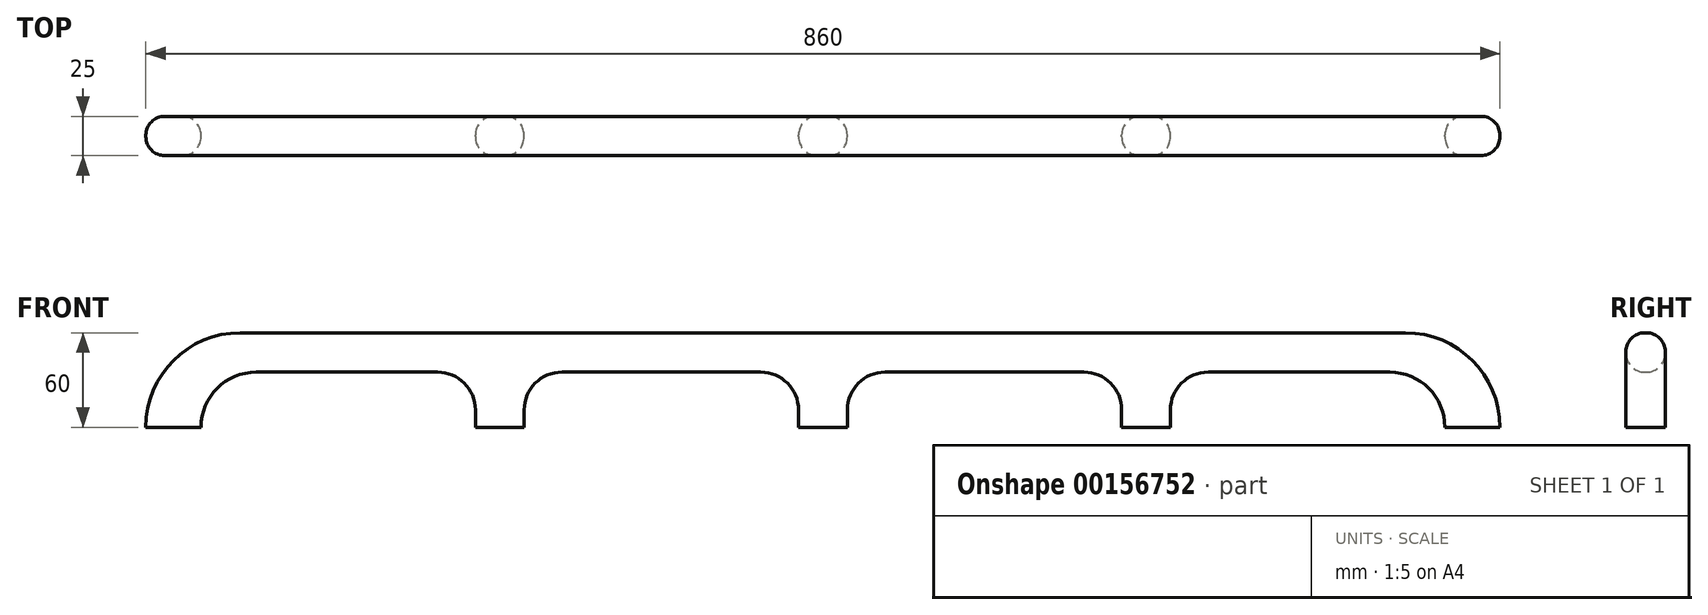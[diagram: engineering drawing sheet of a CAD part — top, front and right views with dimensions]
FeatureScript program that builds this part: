
annotation { "Feature Type Name" : "Feature", "Feature Type Description" : "" }
export const myFeature = defineFeature(function(context is Context, id is Id, definition is map)
    precondition{}
    {
        {
            var Q0;
            Q0=qCreatedBy(makeId("Front.planeOp"),FACE);
            var sketch = newSketch(context, id + "F0", { "sketchPlane" : qUnion([Q0])});
            skLineSegment(sketch, "E0.bottom", {"start": v(-370, 30) * mm, "end": v(0, 30) * mm});
            skLineSegment(sketch, "E0.top", {"start": v(-430, -30) * mm, "end": v(-395, -30) * mm});
            skLineSegment(sketch, "E0.left", {"start": v(-430, -30) * mm, "end": v(-430, -30) * mm});
            skLineSegment(sketch, "E0.right", {"start": v(430, 30) * mm, "end": v(430, -30) * mm, "construction": true});
            skPoint(sketch, "E0.middle", {"position": v(0, 0) * mm});
            skLineSegment(sketch, "E1.0", {"start": v(-395, -30) * mm, "end": v(-395, -30) * mm});
            skLineSegment(sketch, "E2", {"start": v(0, 30) * mm, "end": v(0, -30) * mm, "construction": true});
            skLineSegment(sketch, "E3.0", {"start": v(-15.5, -19) * mm, "end": v(-15.5, -30) * mm, "construction": true});
            skLineSegment(sketch, "E4.0", {"start": v(-360, 5) * mm, "end": v(-244.75, 5) * mm});
            skLineSegment(sketch, "E5.trimOffspring", {"start": v(-15.5, -30) * mm, "end": v(430, -30) * mm, "construction": true});
            skLineSegment(sketch, "E6", {"start": v(-395, -30) * mm, "end": v(-15.5, -30) * mm, "construction": true});
            skLineSegment(sketch, "E7", {"start": v(-205.25, -30) * mm, "end": v(-205.25, 30) * mm, "construction": true});
            skLineSegment(sketch, "E8.0", {"start": v(-220.75, -30) * mm, "end": v(-220.75, -19) * mm});
            skLineSegment(sketch, "E9.0", {"start": v(-189.75, -30) * mm, "end": v(-189.75, -19) * mm});
            skLineSegment(sketch, "E10.trimOffspring", {"start": v(-165.75, 5) * mm, "end": v(-39.5, 5) * mm});
            skLineSegment(sketch, "E11.trimOffspring", {"start": v(0, 5) * mm, "end": v(450, 5) * mm, "construction": true});
            skArc(sketch, "E12.filletArc", {"start": v(-360, 5) * mm, "mid": v(-384.75, -5.25) * mm, "end": v(-395, -30) * mm});
            skArc(sketch, "E13.filletArc", {"start": v(-220.75, -19) * mm, "mid": v(-227.78, -2.03) * mm, "end": v(-244.75, 5) * mm});
            skArc(sketch, "E14.filletArc", {"start": v(-165.75, 5) * mm, "mid": v(-182.72, -2.03) * mm, "end": v(-189.75, -19) * mm});
            skArc(sketch, "E15.filletArc", {"start": v(-15.5, -19) * mm, "mid": v(-22.53, -2.03) * mm, "end": v(-39.5, 5) * mm});
            skPoint(sketch, "E16.visualSharp", {"position": v(-430, 30) * mm});
            skArc(sketch, "E16.filletArc", {"start": v(-370, 30) * mm, "mid": v(-412.43, 12.43) * mm, "end": v(-430, -30) * mm});
            skLineSegment(sketch, "E17", {"start": v(-220.75, -30) * mm, "end": v(-189.75, -30) * mm});
            skLineSegment(sketch, "E18", {"start": v(-15.5, -30) * mm, "end": v(0, -30) * mm});
            skLineSegment(sketch, "E19", {"start": v(-15.5, -19) * mm, "end": v(-15.5, -30) * mm});
            skLineSegment(sketch, "E20.MirrorCS", {"start": v(370, 30) * mm, "end": v(0, 30) * mm});
            skArc(sketch, "E21.MirrorCS", {"start": v(370, 30) * mm, "mid": v(412.43, 12.43) * mm, "end": v(430, -30) * mm});
            skLineSegment(sketch, "E22.MirrorCS", {"start": v(430, -30) * mm, "end": v(395, -30) * mm});
            skArc(sketch, "E23.MirrorCS", {"start": v(360, 5) * mm, "mid": v(384.75, -5.25) * mm, "end": v(395, -30) * mm});
            skLineSegment(sketch, "E24.MirrorCS", {"start": v(360, 5) * mm, "end": v(244.75, 5) * mm});
            skArc(sketch, "E25.MirrorCS", {"start": v(220.75, -19) * mm, "mid": v(227.78, -2.03) * mm, "end": v(244.75, 5) * mm});
            skLineSegment(sketch, "E26.MirrorCS", {"start": v(220.75, -30) * mm, "end": v(220.75, -19) * mm});
            skLineSegment(sketch, "E27.MirrorCS", {"start": v(220.75, -30) * mm, "end": v(189.75, -30) * mm});
            skLineSegment(sketch, "E28.MirrorCS", {"start": v(189.75, -30) * mm, "end": v(189.75, -19) * mm});
            skArc(sketch, "E29.MirrorCS", {"start": v(165.75, 5) * mm, "mid": v(182.72, -2.03) * mm, "end": v(189.75, -19) * mm});
            skLineSegment(sketch, "E30.MirrorCS", {"start": v(165.75, 5) * mm, "end": v(39.5, 5) * mm});
            skArc(sketch, "E31.MirrorCS", {"start": v(15.5, -19) * mm, "mid": v(22.53, -2.03) * mm, "end": v(39.5, 5) * mm});
            skLineSegment(sketch, "E32.MirrorCS", {"start": v(15.5, -19) * mm, "end": v(15.5, -30) * mm});
            skLineSegment(sketch, "E33.MirrorCS", {"start": v(15.5, -30) * mm, "end": v(0, -30) * mm});
            skSolve(sketch);
        }
        {
            var Q0;
            Q0=makeQuery(id+"F0.imprint","IMPRINT",FACE,{"disambiguationData":[TD([[makeQuery(id+"F0.imprint","IMPRINT",EDGE,{"derivedFrom":sQuery(id+"F0.wireOp",EDGE,"E0.bottom")}),-1.0]])]});
            extrude(context, id + "F1", {"entities" : qUnion([Q0]), "depth" : 25 * mm, "symmetric" : true});
        }
        {
            var Q0;
            Q0=makeQuery(id+"F1.opExtrude","CAP_EDGE",EDGE,{"disambiguationData":[OSD([sQuery(id+"F0.wireOp",EDGE,"E12.filletArc")])],"isStart":false});
            var Q1;
            Q1=makeQuery(id+"F1.opExtrude","CAP_EDGE",EDGE,{"disambiguationData":[OSD([sQuery(id+"F0.wireOp",EDGE,"E14.filletArc")])],"isStart":false});
            var Q2;
            Q2=makeQuery(id+"F1.opExtrude","CAP_EDGE",EDGE,{"disambiguationData":[OSD([sQuery(id+"F0.wireOp",EDGE,"E31.MirrorCS")])],"isStart":false});
            var Q3;
            Q3=makeQuery(id+"F1.opExtrude","CAP_EDGE",EDGE,{"disambiguationData":[OSD([sQuery(id+"F0.wireOp",EDGE,"E25.MirrorCS")])],"isStart":false});
            var Q4;
            Q4=makeQuery(id+"F1.opExtrude","CAP_EDGE",EDGE,{"disambiguationData":[OSD([sQuery(id+"F0.wireOp",EDGE,"E21.MirrorCS")])],"isStart":false});
            var Q5;
            Q5=makeQuery(id+"F1.opExtrude","CAP_EDGE",EDGE,{"disambiguationData":[OSD([sQuery(id+"F0.wireOp",EDGE,"E16.filletArc")])],"isStart":true});
            var Q6;
            Q6=makeQuery(id+"F1.opExtrude","CAP_EDGE",EDGE,{"disambiguationData":[OSD([sQuery(id+"F0.wireOp",EDGE,"E13.filletArc")])],"isStart":true});
            var Q7;
            Q7=makeQuery(id+"F1.opExtrude","CAP_EDGE",EDGE,{"disambiguationData":[OSD([sQuery(id+"F0.wireOp",EDGE,"E15.filletArc")])],"isStart":true});
            var Q8;
            Q8=makeQuery(id+"F1.opExtrude","CAP_EDGE",EDGE,{"disambiguationData":[OSD([sQuery(id+"F0.wireOp",EDGE,"E29.MirrorCS")])],"isStart":true});
            var Q9;
            Q9=makeQuery(id+"F1.opExtrude","CAP_EDGE",EDGE,{"disambiguationData":[OSD([sQuery(id+"F0.wireOp",EDGE,"E23.MirrorCS")])],"isStart":true});
            fillet(context, id + "F2", {"entities" : qUnion([Q0, Q1, Q2, Q3, Q4, Q5, Q6, Q7, Q8, Q9]), "radius" : 12 * mm, "tangentPropagation" : true, "allowEdgeOverflow" : false});
        }
    });
